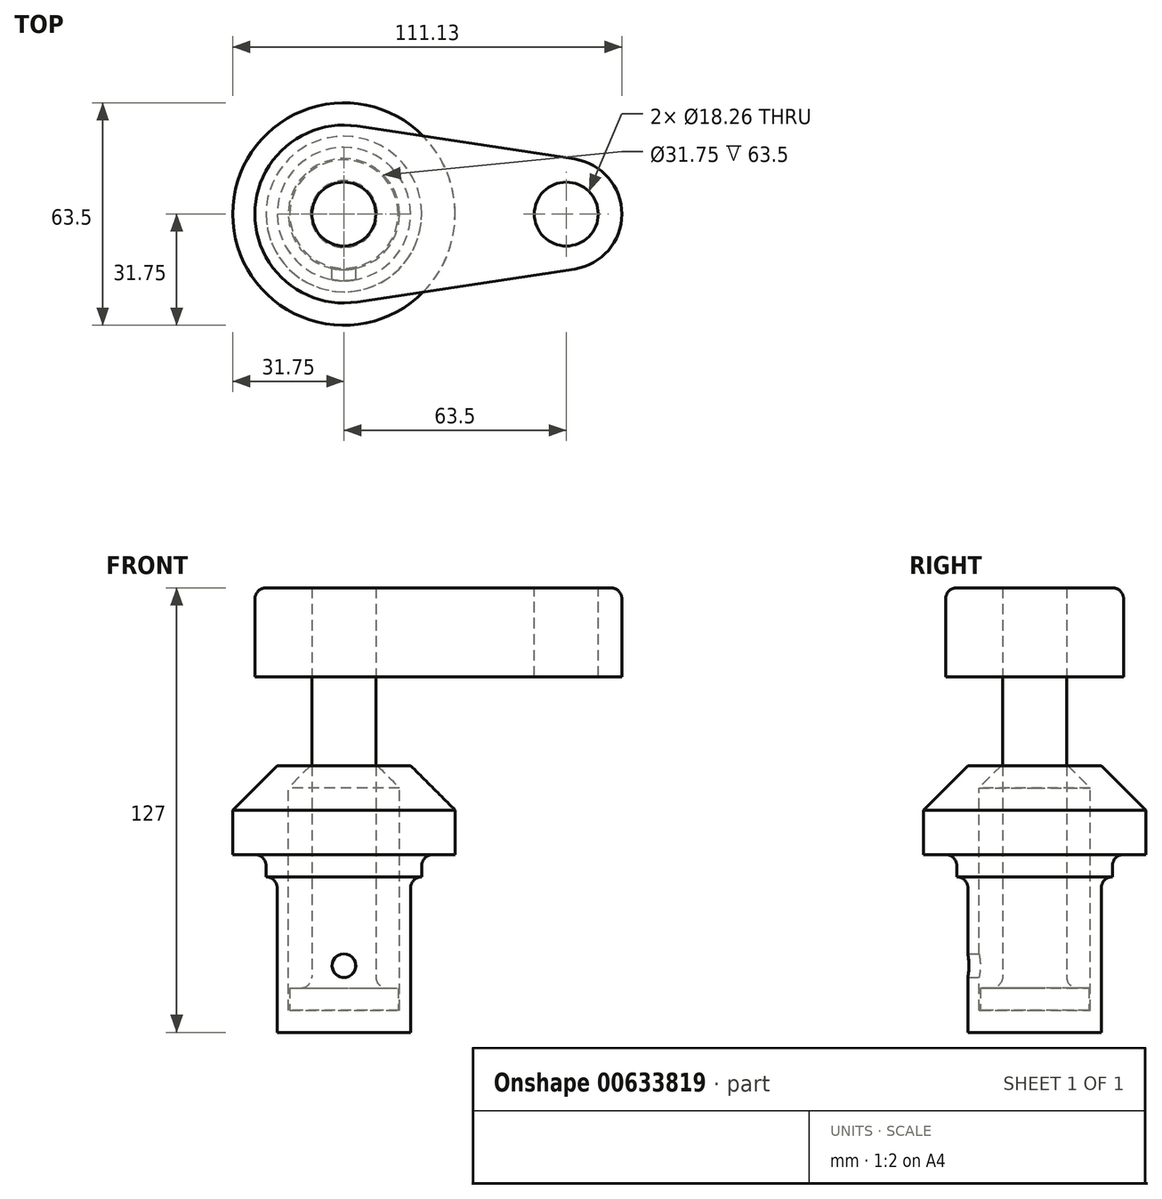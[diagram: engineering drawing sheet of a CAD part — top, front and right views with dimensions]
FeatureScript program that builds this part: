
annotation { "Feature Type Name" : "Feature", "Feature Type Description" : "" }
export const myFeature = defineFeature(function(context is Context, id is Id, definition is map)
    precondition{}
    {
        {
            var Q0;
            Q0=qCreatedBy(makeId("Front.planeOp"),FACE);
            var sketch = newSketch(context, id + "F0", { "sketchPlane" : qUnion([Q0])});
            skLineSegment(sketch, "E0", {"start": v(0, 0) * mm, "end": v(0, 76.2) * mm});
            skLineSegment(sketch, "E1", {"start": v(0, 76.2) * mm, "end": v(19.05, 76.2) * mm});
            skLineSegment(sketch, "E2", {"start": v(19.05, 76.2) * mm, "end": v(31.75, 63.5) * mm});
            skLineSegment(sketch, "E3", {"start": v(31.75, 63.5) * mm, "end": v(31.75, 50.8) * mm});
            skLineSegment(sketch, "E4", {"start": v(31.75, 50.8) * mm, "end": v(22.23, 50.8) * mm});
            skLineSegment(sketch, "E5", {"start": v(22.23, 50.8) * mm, "end": v(22.23, 44.45) * mm});
            skLineSegment(sketch, "E6", {"start": v(22.23, 44.45) * mm, "end": v(19.05, 44.45) * mm});
            skLineSegment(sketch, "E7", {"start": v(19.05, 44.45) * mm, "end": v(19.05, 0) * mm});
            skLineSegment(sketch, "E8", {"start": v(19.05, 0) * mm, "end": v(0, 0) * mm});
            skLineSegment(sketch, "E9", {"start": v(9.53, 76.2) * mm, "end": v(15.88, 69.85) * mm});
            skLineSegment(sketch, "E10", {"start": v(15.88, 69.85) * mm, "end": v(15.88, 6.35) * mm});
            skLineSegment(sketch, "E11", {"start": v(15.88, 6.35) * mm, "end": v(0, 6.35) * mm});
            skLineSegment(sketch, "E12", {"start": v(0, 76.2) * mm, "end": v(0, 94.95) * mm, "construction": true});
            skLineSegment(sketch, "E13", {"start": v(0, 76.2) * mm, "end": v(0, 127) * mm});
            skLineSegment(sketch, "E14", {"start": v(0, 127) * mm, "end": v(9.13, 127) * mm});
            skLineSegment(sketch, "E15", {"start": v(9.13, 127) * mm, "end": v(9.13, 12.7) * mm});
            skLineSegment(sketch, "E16", {"start": v(9.13, 12.7) * mm, "end": v(15.48, 12.7) * mm});
            skLineSegment(sketch, "E17", {"start": v(15.48, 12.7) * mm, "end": v(15.48, 6.35) * mm});
            skSolve(sketch);
        }
        {
            var Q0;
            {var subQ4=sQuery(id+"F0.wireOp",EDGE,"E2");Q0=makeQuery(id+"F0.imprint","IMPRINT",FACE,{"disambiguationData":[TD([[makeQuery(id+"F0.imprint","IMPRINT",EDGE,{"derivedFrom":subQ4}),-1.0]])]});}
            var Q1;
            Q1=sQuery(id+"F0.wireOp",EDGE,"E0");
            revolve(context, id + "F1", {"entities" : qUnion([Q0]), "axis" : qUnion([Q1]), "revolveType" : RevolveType.FULL, "oppositeDirection" : true});
        }
        {
            var Q0;
            {var subQ0=sQuery(id+"F0.wireOp",EDGE,"E13");Q0=makeQuery(id+"F0.imprint","IMPRINT",FACE,{"disambiguationData":[TD([[makeQuery(id+"F0.imprint","IMPRINT",EDGE,{"derivedFrom":subQ0}),-1.0]])]});}
            var Q1;
            {var subQ0=sQuery(id+"F0.wireOp",EDGE,"E16");Q1=makeQuery(id+"F0.imprint","IMPRINT",FACE,{"disambiguationData":[TD([[makeQuery(id+"F0.imprint","IMPRINT",EDGE,{"derivedFrom":subQ0}),-1.0]])]});}
            var Q2;
            Q2=sQuery(id+"F0.wireOp",EDGE,"E13");
            revolve(context, id + "F2", {"entities" : qUnion([Q0, Q1]), "axis" : qUnion([Q2]), "revolveType" : RevolveType.FULL});
        }
        {
            var Q0;
            Q0=makeQuery(id+"F2.opRevolve","SWEPT_FACE",FACE,{"disambiguationData":[OSD([sQuery(id+"F0.wireOp",EDGE,"E14")])]});
            var sketch = newSketch(context, id + "F3", { "sketchPlane" : qUnion([Q0])});
            skCircle(sketch, "E18", {"center": v(0, 0) * mm, "radius": 25.4 * mm});
            skCircle(sketch, "E19", {"center": v(63.5, 0) * mm, "radius": 15.88 * mm});
            skLineSegment(sketch, "E20", {"start": v(3.81, 25.11) * mm, "end": v(65.88, 15.7) * mm});
            skLineSegment(sketch, "E21", {"start": v(3.8, -25.11) * mm, "end": v(65.88, -15.7) * mm});
            skCircle(sketch, "E22.0", {"center": v(0, 0) * mm, "radius": 9.13 * mm});
            skCircle(sketch, "E23", {"center": v(63.5, 0) * mm, "radius": 9.13 * mm});
            skSolve(sketch);
        }
        {
            var Q0;
            Q0 = qSketchRegion(id + "F3", true);
            var Q1;
            Q1=makeQuery(id+"F1.opRevolve","SWEPT_FACE",FACE,{"disambiguationData":[OSD([sQuery(id+"F0.wireOp",EDGE,"E1")])]});
            extrude(context, id + "F4", {"entities" : qUnion([Q0]), "oppositeDirection" : true, "depth" : 25.4 * mm, "endBoundEntityFace" : qUnion([Q1]), "offsetDistance" : 1.59 * mm});
        }
        {
            var Q0;
            Q0=qCreatedBy(makeId("Front.planeOp"),FACE);
            var sketch = newSketch(context, id + "F5", { "sketchPlane" : qUnion([Q0])});
            skPoint(sketch, "E24", {"position": v(0, 19.05) * mm});
            skSolve(sketch);
        }
        {
            var Q0;
            Q0=sQuery(id+"F5.wireOp",VERTEX,"E24");
            var Q1;
            Q1=makeQuery(id+"F1.opRevolve","SWEPT_BODY",BODY,{"disambiguationData":[OSD([sQuery(id+"F0.wireOp",EDGE,"E0"),sQuery(id+"F0.wireOp",EDGE,"E1"),sQuery(id+"F0.wireOp",EDGE,"E2"),sQuery(id+"F0.wireOp",EDGE,"E3"),sQuery(id+"F0.wireOp",EDGE,"E4"),sQuery(id+"F0.wireOp",EDGE,"E5"),sQuery(id+"F0.wireOp",EDGE,"E6"),sQuery(id+"F0.wireOp",EDGE,"E7"),sQuery(id+"F0.wireOp",EDGE,"E8"),sQuery(id+"F0.wireOp",EDGE,"E9"),sQuery(id+"F0.wireOp",EDGE,"E10"),sQuery(id+"F0.wireOp",EDGE,"E11")])]});
            hole(context, id + "F6", {"style" : HoleStyle.SIMPLE, "endStyle" : HoleEndStyle.THROUGH, "oppositeDirection" : true, "standardTappedOrClearance" : lookupTablePath({ "standard" : "ANSI", "fit" : "Normal (ASME)", "size" : "1/4", "type" : "Clearance" }), "standardBlindInLast" : lookupTablePath({ "fit" : "Free", "standard" : "ANSI", "size" : "1/4", "type" : "Clearance" }), "holeDiameter" : 6.76 * mm, "majorDiameter" : 6.35 * mm, "tappedDepth" : 14.3 * mm, "tapClearance" : 3, "locations" : qUnion([Q0]), "scope" : qUnion([Q1])});
        }
        {
            var Q0;
            Q0=makeQuery(id+"F4.opExtrude","CAP_EDGE",EDGE,{"disambiguationData":[OSD([sQuery(id+"F3.wireOp",EDGE,"E20")])],"isStart":true});
            var Q1;
            Q1=makeQuery(id+"F1.opRevolve","SWEPT_EDGE",EDGE,{"disambiguationData":[OSD([sQuery(id+"F0.wireOp",EDGE,"E6"),sQuery(id+"F0.wireOp",EDGE,"E7")])]});
            var Q2;
            Q2=makeQuery(id+"F1.opRevolve","SWEPT_EDGE",EDGE,{"disambiguationData":[OSD([sQuery(id+"F0.wireOp",EDGE,"E4"),sQuery(id+"F0.wireOp",EDGE,"E5")])]});
            var Q3;
            Q3=makeQuery(id+"F2.opRevolve","SWEPT_EDGE",EDGE,{"disambiguationData":[OSD([sQuery(id+"F0.wireOp",EDGE,"E15"),sQuery(id+"F0.wireOp",EDGE,"E16")])]});
            fillet(context, id + "F7", {"entities" : qUnion([Q0, Q1, Q2, Q3]), "radius" : 3.17 * mm, "tangentPropagation" : true, "allowEdgeOverflow" : false});
        }
    });
